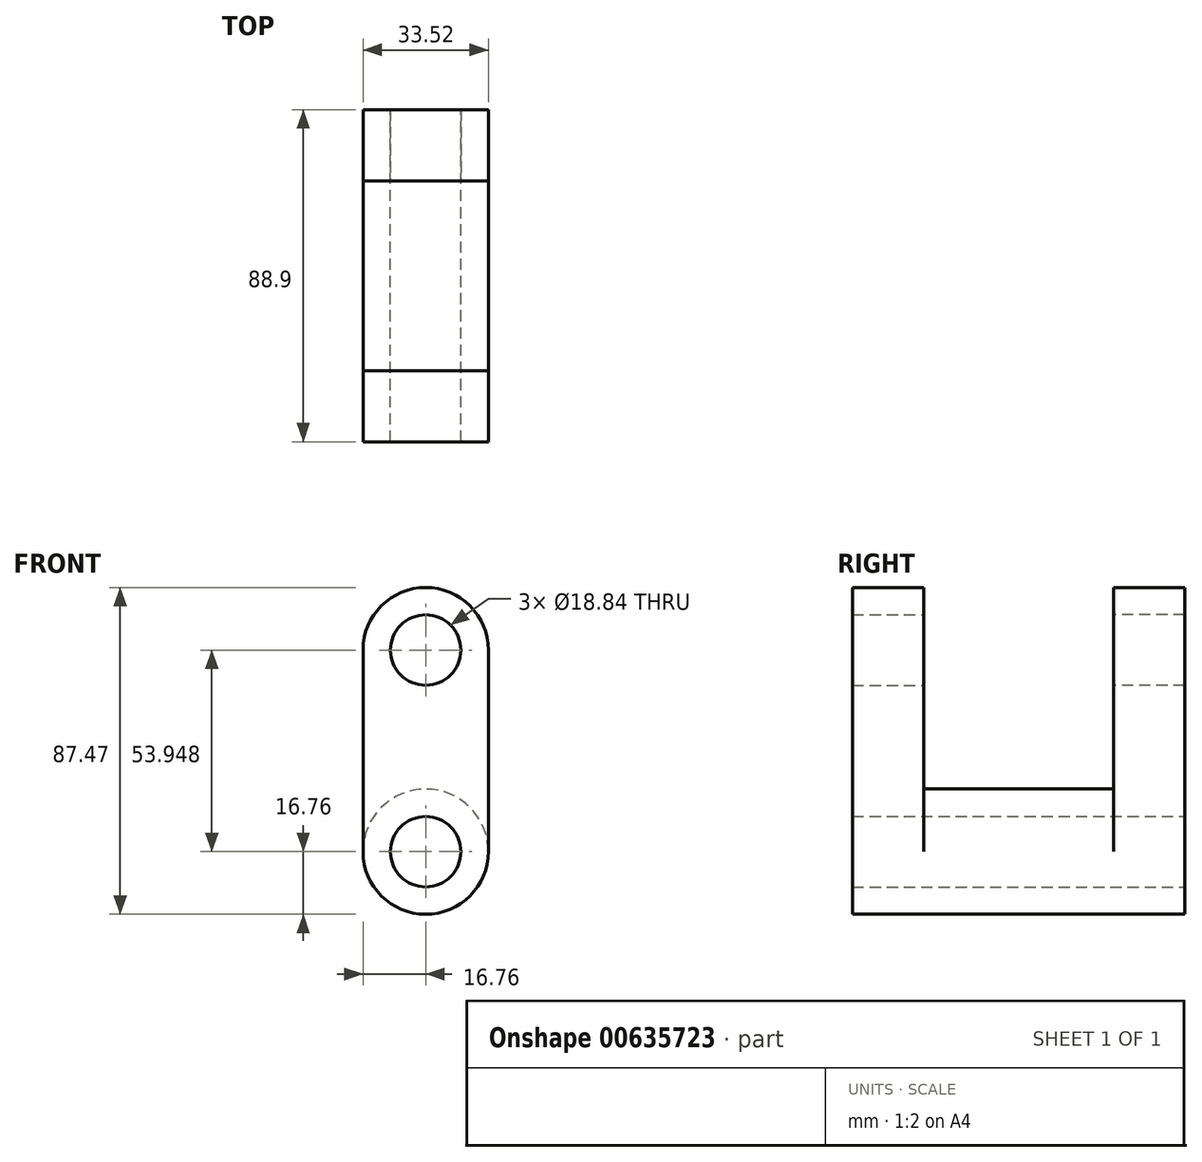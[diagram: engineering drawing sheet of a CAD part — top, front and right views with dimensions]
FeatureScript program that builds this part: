
annotation { "Feature Type Name" : "Feature", "Feature Type Description" : "" }
export const myFeature = defineFeature(function(context is Context, id is Id, definition is map)
    precondition{}
    {
        {
            var Q0;
            Q0=qCreatedBy(makeId("Front.planeOp"),FACE);
            var sketch = newSketch(context, id + "F0", { "sketchPlane" : qUnion([Q0])});
            skCircle(sketch, "E0", {"center": v(0, 0) * mm, "radius": 9.42 * mm});
            skCircle(sketch, "E1", {"center": v(0, 53.95) * mm, "radius": 9.42 * mm});
            skCircle(sketch, "E2", {"center": v(0, 0) * mm, "radius": 16.76 * mm});
            skCircle(sketch, "E3", {"center": v(0, 53.95) * mm, "radius": 16.76 * mm});
            skLineSegment(sketch, "E4", {"start": v(-16.76, 53.95) * mm, "end": v(-16.76, 0) * mm});
            skLineSegment(sketch, "E5", {"start": v(16.76, 53.95) * mm, "end": v(16.76, 0) * mm});
            skSolve(sketch);
        }
        {
            var Q0;
            Q0=makeQuery(id+"F0.imprint","IMPRINT",FACE,{"disambiguationData":[TD([[makeQuery(id+"F0.imprint","IMPRINT",EDGE,{"derivedFrom":sQuery(id+"F0.wireOp",EDGE,"E1")}),-1.0]])]});
            var Q1;
            {var subQ0=sQuery(id+"F0.wireOp",EDGE,"E4");Q1=makeQuery(id+"F0.imprint","IMPRINT",FACE,{"disambiguationData":[TD([[makeQuery(id+"F0.imprint","IMPRINT",EDGE,{"derivedFrom":subQ0}),1.0]])]});}
            var Q2;
            Q2=makeQuery(id+"F0.imprint","IMPRINT",FACE,{"disambiguationData":[TD([[makeQuery(id+"F0.imprint","IMPRINT",EDGE,{"derivedFrom":sQuery(id+"F0.wireOp",EDGE,"E0")}),-1.0]])]});
            extrude(context, id + "F1", {"entities" : qUnion([Q0, Q1, Q2]), "depth" : 19.05 * mm, "offsetDistance" : 25.4 * mm});
        }
        {
            var Q0;
            Q0=makeQuery(id+"F0.imprint","IMPRINT",FACE,{"disambiguationData":[TD([[makeQuery(id+"F0.imprint","IMPRINT",EDGE,{"derivedFrom":sQuery(id+"F0.wireOp",EDGE,"E0")}),-1.0]])]});
            extrude(context, id + "F2", {"entities" : qUnion([Q0]), "operationType" : NewBodyOperationType.ADD, "oppositeDirection" : true, "depth" : 25.4 * mm, "offsetDistance" : 25.4 * mm});
        }
        {
            var Q0;
            Q0=makeQuery(id+"F1.opExtrude","SWEPT_BODY",BODY,{"disambiguationData":[OSD([sQuery(id+"F0.wireOp",EDGE,"E0"),sQuery(id+"F0.wireOp",EDGE,"E1"),sQuery(id+"F0.wireOp",EDGE,"E2"),sQuery(id+"F0.wireOp",EDGE,"E3"),sQuery(id+"F0.wireOp",EDGE,"E4"),sQuery(id+"F0.wireOp",EDGE,"E5")])]});
            var Q1;
            Q1=makeQuery(id+"F2.opExtrude","CAP_FACE",FACE,{"disambiguationData":[OSD([sQuery(id+"F0.wireOp",EDGE,"E0"),sQuery(id+"F0.wireOp",EDGE,"E2")])],"isStart":false});
            mirror(context, id + "F3", {"operationType" : NewBodyOperationType.ADD, "entities" : qUnion([Q0]), "mirrorPlane" : qUnion([Q1])});
        }
    });
